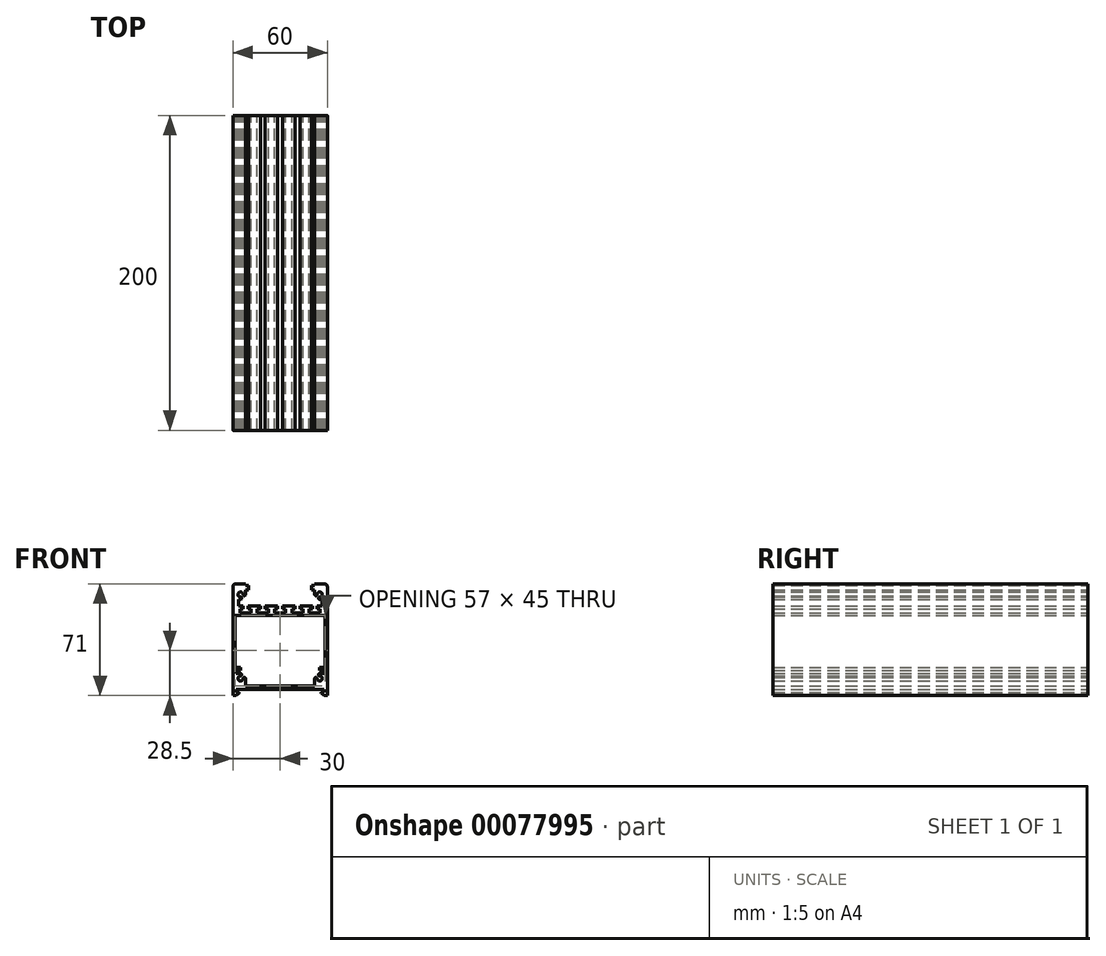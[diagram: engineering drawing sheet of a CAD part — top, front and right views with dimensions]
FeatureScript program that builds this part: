
annotation { "Feature Type Name" : "Feature", "Feature Type Description" : "" }
export const myFeature = defineFeature(function(context is Context, id is Id, definition is map)
    precondition{}
    {
        {
            var Q0;
            Q0=qCreatedBy(makeId("Front.planeOp"),FACE);
            var sketch = newSketch(context, id + "F0", { "sketchPlane" : qUnion([Q0])});
            skLineSegment(sketch, "E0", {"start": v(25.9, -50.3) * mm, "end": v(-25.9, -50.3) * mm});
            skArc(sketch, "E1", {"start": v(-22, -41.64) * mm, "mid": v(-22.75, -40.9) * mm, "end": v(-23.5, -41.64) * mm});
            skLineSegment(sketch, "E2", {"start": v(-22, -41.64) * mm, "end": v(-22, -46.5) * mm});
            skLineSegment(sketch, "E3", {"start": v(-22, -46.5) * mm, "end": v(22, -46.5) * mm});
            skLineSegment(sketch, "E4", {"start": v(22, -46.5) * mm, "end": v(22, -41.64) * mm});
            skArc(sketch, "E5", {"start": v(23.5, -41.64) * mm, "mid": v(22.75, -40.9) * mm, "end": v(22, -41.64) * mm});
            skArc(sketch, "E6", {"start": v(23.5, -41.64) * mm, "mid": v(26.31, -42.81) * mm, "end": v(25.14, -40) * mm});
            skArc(sketch, "E7", {"start": v(25.14, -38.5) * mm, "mid": v(24.4, -39.25) * mm, "end": v(25.14, -40) * mm});
            skLineSegment(sketch, "E8", {"start": v(25.14, -38.5) * mm, "end": v(28, -38.5) * mm});
            skLineSegment(sketch, "E9", {"start": v(28, -38.5) * mm, "end": v(28, -36.5) * mm});
            skLineSegment(sketch, "E10", {"start": v(28, -36.5) * mm, "end": v(25, -36.5) * mm});
            skLineSegment(sketch, "E11", {"start": v(25, -36.5) * mm, "end": v(25, -34.5) * mm});
            skLineSegment(sketch, "E12", {"start": v(25, -34.5) * mm, "end": v(28.5, -34.5) * mm});
            skLineSegment(sketch, "E13", {"start": v(28.5, -34.5) * mm, "end": v(28.5, -1.5) * mm});
            skLineSegment(sketch, "E14", {"start": v(28.5, -1.5) * mm, "end": v(-28.5, -1.5) * mm});
            skLineSegment(sketch, "E15", {"start": v(-28.5, -1.5) * mm, "end": v(-28.5, -34.5) * mm});
            skLineSegment(sketch, "E16", {"start": v(-28.5, -34.5) * mm, "end": v(-25, -34.5) * mm});
            skLineSegment(sketch, "E17", {"start": v(-25, -34.5) * mm, "end": v(-25, -36.5) * mm});
            skLineSegment(sketch, "E18", {"start": v(-25, -36.5) * mm, "end": v(-28, -36.5) * mm});
            skLineSegment(sketch, "E19", {"start": v(-28, -36.5) * mm, "end": v(-28, -38.5) * mm});
            skLineSegment(sketch, "E20", {"start": v(-28, -38.5) * mm, "end": v(-25.14, -38.5) * mm});
            skArc(sketch, "E21", {"start": v(-25.14, -40) * mm, "mid": v(-24.4, -39.25) * mm, "end": v(-25.14, -38.5) * mm});
            skArc(sketch, "E22", {"start": v(-25.14, -40) * mm, "mid": v(-26.31, -42.81) * mm, "end": v(-23.5, -41.64) * mm});
            skLineSegment(sketch, "E23", {"start": v(-22, 18.5) * mm, "end": v(-28, 18.5) * mm});
            skLineSegment(sketch, "E24", {"start": v(-22, 17.5) * mm, "end": v(-22, 18.5) * mm});
            skLineSegment(sketch, "E25", {"start": v(-20, 17.5) * mm, "end": v(-22, 17.5) * mm});
            skLineSegment(sketch, "E26", {"start": v(-20, 14.5) * mm, "end": v(-20, 17.5) * mm});
            skLineSegment(sketch, "E27", {"start": v(-22, 14.5) * mm, "end": v(-20, 14.5) * mm});
            skLineSegment(sketch, "E28", {"start": v(-22, 11.64) * mm, "end": v(-22, 14.5) * mm});
            skArc(sketch, "E29", {"start": v(-23.5, 11.64) * mm, "mid": v(-22.75, 10.9) * mm, "end": v(-22, 11.64) * mm});
            skArc(sketch, "E30", {"start": v(-23.5, 11.64) * mm, "mid": v(-26.31, 12.81) * mm, "end": v(-25.14, 10) * mm});
            skArc(sketch, "E31", {"start": v(-25.14, 8.5) * mm, "mid": v(-24.4, 9.25) * mm, "end": v(-25.14, 10) * mm});
            skLineSegment(sketch, "E32", {"start": v(-26.5, 8.5) * mm, "end": v(-25.14, 8.5) * mm});
            skLineSegment(sketch, "E33", {"start": v(-26.5, 4.5) * mm, "end": v(-26.5, 8.5) * mm});
            skLineSegment(sketch, "E34", {"start": v(-23.5, 4.5) * mm, "end": v(-26.5, 4.5) * mm});
            skLineSegment(sketch, "E35", {"start": v(-23.5, 2.5) * mm, "end": v(-23.5, 4.5) * mm});
            skLineSegment(sketch, "E36", {"start": v(-25.5, 2.5) * mm, "end": v(-23.5, 2.5) * mm});
            skLineSegment(sketch, "E37", {"start": v(-25.5, 0) * mm, "end": v(-25.5, 2.5) * mm});
            skLineSegment(sketch, "E38", {"start": v(-18.5, 0) * mm, "end": v(-25.5, 0) * mm});
            skLineSegment(sketch, "E39", {"start": v(-18.5, 2.5) * mm, "end": v(-18.5, 0) * mm});
            skLineSegment(sketch, "E40", {"start": v(-20.5, 2.5) * mm, "end": v(-18.5, 2.5) * mm});
            skLineSegment(sketch, "E41", {"start": v(-20.5, 4.5) * mm, "end": v(-20.5, 2.5) * mm});
            skLineSegment(sketch, "E42", {"start": v(-12.5, 4.5) * mm, "end": v(-20.5, 4.5) * mm});
            skLineSegment(sketch, "E43", {"start": v(-12.5, 2.5) * mm, "end": v(-12.5, 4.5) * mm});
            skLineSegment(sketch, "E44", {"start": v(-14.5, 2.5) * mm, "end": v(-12.5, 2.5) * mm});
            skLineSegment(sketch, "E45", {"start": v(-14.5, 0) * mm, "end": v(-14.5, 2.5) * mm});
            skLineSegment(sketch, "E46", {"start": v(-7.5, 0) * mm, "end": v(-14.5, 0) * mm});
            skLineSegment(sketch, "E47", {"start": v(-7.5, 2.5) * mm, "end": v(-7.5, 0) * mm});
            skLineSegment(sketch, "E48", {"start": v(-9.5, 2.5) * mm, "end": v(-7.5, 2.5) * mm});
            skLineSegment(sketch, "E49", {"start": v(-9.5, 4.5) * mm, "end": v(-9.5, 2.5) * mm});
            skLineSegment(sketch, "E50", {"start": v(-1.5, 4.5) * mm, "end": v(-9.5, 4.5) * mm});
            skLineSegment(sketch, "E51", {"start": v(-1.5, 2.5) * mm, "end": v(-1.5, 4.5) * mm});
            skLineSegment(sketch, "E52", {"start": v(-3.5, 2.5) * mm, "end": v(-1.5, 2.5) * mm});
            skLineSegment(sketch, "E53", {"start": v(-3.5, 0) * mm, "end": v(-3.5, 2.5) * mm});
            skLineSegment(sketch, "E54", {"start": v(3.5, 0) * mm, "end": v(-3.5, 0) * mm});
            skLineSegment(sketch, "E55", {"start": v(3.5, 2.5) * mm, "end": v(3.5, 0) * mm});
            skLineSegment(sketch, "E56", {"start": v(1.5, 2.5) * mm, "end": v(3.5, 2.5) * mm});
            skLineSegment(sketch, "E57", {"start": v(1.5, 4.5) * mm, "end": v(1.5, 2.5) * mm});
            skLineSegment(sketch, "E58", {"start": v(9.5, 4.5) * mm, "end": v(1.5, 4.5) * mm});
            skLineSegment(sketch, "E59", {"start": v(9.5, 2.5) * mm, "end": v(9.5, 4.5) * mm});
            skLineSegment(sketch, "E60", {"start": v(7.5, 2.5) * mm, "end": v(9.5, 2.5) * mm});
            skLineSegment(sketch, "E61", {"start": v(7.5, 0) * mm, "end": v(7.5, 2.5) * mm});
            skLineSegment(sketch, "E62", {"start": v(14.5, 0) * mm, "end": v(7.5, 0) * mm});
            skLineSegment(sketch, "E63", {"start": v(14.5, 2.5) * mm, "end": v(14.5, 0) * mm});
            skLineSegment(sketch, "E64", {"start": v(12.5, 2.5) * mm, "end": v(14.5, 2.5) * mm});
            skLineSegment(sketch, "E65", {"start": v(12.5, 4.5) * mm, "end": v(12.5, 2.5) * mm});
            skLineSegment(sketch, "E66", {"start": v(20.5, 4.5) * mm, "end": v(12.5, 4.5) * mm});
            skLineSegment(sketch, "E67", {"start": v(20.5, 2.5) * mm, "end": v(20.5, 4.5) * mm});
            skLineSegment(sketch, "E68", {"start": v(18.5, 2.5) * mm, "end": v(20.5, 2.5) * mm});
            skLineSegment(sketch, "E69", {"start": v(18.5, 0) * mm, "end": v(18.5, 2.5) * mm});
            skLineSegment(sketch, "E70", {"start": v(25.5, 0) * mm, "end": v(18.5, 0) * mm});
            skLineSegment(sketch, "E71", {"start": v(25.5, 2.5) * mm, "end": v(25.5, 0) * mm});
            skLineSegment(sketch, "E72", {"start": v(23.5, 2.5) * mm, "end": v(25.5, 2.5) * mm});
            skLineSegment(sketch, "E73", {"start": v(23.5, 4.5) * mm, "end": v(23.5, 2.5) * mm});
            skLineSegment(sketch, "E74", {"start": v(26.5, 4.5) * mm, "end": v(23.5, 4.5) * mm});
            skLineSegment(sketch, "E75", {"start": v(26.5, 8.5) * mm, "end": v(26.5, 4.5) * mm});
            skLineSegment(sketch, "E76", {"start": v(25.14, 8.5) * mm, "end": v(26.5, 8.5) * mm});
            skArc(sketch, "E77", {"start": v(25.14, 10) * mm, "mid": v(24.4, 9.25) * mm, "end": v(25.14, 8.5) * mm});
            skArc(sketch, "E78", {"start": v(25.14, 10) * mm, "mid": v(26.31, 12.81) * mm, "end": v(23.5, 11.64) * mm});
            skArc(sketch, "E79", {"start": v(22, 11.64) * mm, "mid": v(22.75, 10.9) * mm, "end": v(23.5, 11.64) * mm});
            skLineSegment(sketch, "E80", {"start": v(22, 14.5) * mm, "end": v(22, 11.64) * mm});
            skLineSegment(sketch, "E81", {"start": v(20, 14.5) * mm, "end": v(22, 14.5) * mm});
            skLineSegment(sketch, "E82", {"start": v(20, 17.5) * mm, "end": v(20, 14.5) * mm});
            skLineSegment(sketch, "E83", {"start": v(22, 17.5) * mm, "end": v(20, 17.5) * mm});
            skLineSegment(sketch, "E84", {"start": v(22, 18.5) * mm, "end": v(22, 17.5) * mm});
            skLineSegment(sketch, "E85", {"start": v(28, 18.5) * mm, "end": v(22, 18.5) * mm});
            skArc(sketch, "E86", {"start": v(30, 16.5) * mm, "mid": v(29.41, 17.91) * mm, "end": v(28, 18.5) * mm});
            skLineSegment(sketch, "E87", {"start": v(30, -52.5) * mm, "end": v(30, 16.5) * mm});
            skLineSegment(sketch, "E88", {"start": v(28, -52.5) * mm, "end": v(30, -52.5) * mm});
            skLineSegment(sketch, "E89", {"start": v(26.17, -51.23) * mm, "end": v(28, -52.5) * mm});
            skArc(sketch, "E90", {"start": v(26.4, -50.5) * mm, "mid": v(26.02, -50.78) * mm, "end": v(26.17, -51.23) * mm});
            skLineSegment(sketch, "E91", {"start": v(28, -50.5) * mm, "end": v(26.4, -50.5) * mm});
            skLineSegment(sketch, "E92", {"start": v(28, -48.5) * mm, "end": v(28, -50.5) * mm});
            skLineSegment(sketch, "E93", {"start": v(-28, -48.5) * mm, "end": v(28, -48.5) * mm});
            skLineSegment(sketch, "E94", {"start": v(-28, -50.5) * mm, "end": v(-28, -48.5) * mm});
            skLineSegment(sketch, "E95", {"start": v(-26.4, -50.5) * mm, "end": v(-28, -50.5) * mm});
            skArc(sketch, "E96", {"start": v(-26.17, -51.23) * mm, "mid": v(-26.02, -50.78) * mm, "end": v(-26.4, -50.5) * mm});
            skLineSegment(sketch, "E97", {"start": v(-28, -52.5) * mm, "end": v(-26.17, -51.23) * mm});
            skLineSegment(sketch, "E98", {"start": v(-30, -52.5) * mm, "end": v(-28, -52.5) * mm});
            skLineSegment(sketch, "E99", {"start": v(-30, 16.5) * mm, "end": v(-30, -52.5) * mm});
            skArc(sketch, "E100", {"start": v(-28, 18.5) * mm, "mid": v(-29.41, 17.91) * mm, "end": v(-30, 16.5) * mm});
            skLineSegment(sketch, "E101", {"start": v(-12, -57.35) * mm, "end": v(12, -57.35) * mm});
            skLineSegment(sketch, "E102", {"start": v(-7.75, -65.35) * mm, "end": v(-12, -65.35) * mm});
            skLineSegment(sketch, "E103", {"start": v(-7.75, -67.35) * mm, "end": v(-7.75, -65.35) * mm});
            skLineSegment(sketch, "E104", {"start": v(-15.25, -67.35) * mm, "end": v(-7.75, -67.35) * mm});
            skLineSegment(sketch, "E105", {"start": v(-15.25, -65.35) * mm, "end": v(-15.25, -67.35) * mm});
            skLineSegment(sketch, "E106", {"start": v(-12, -65.35) * mm, "end": v(-12, -57.35) * mm});
            skLineSegment(sketch, "E107", {"start": v(-13.78, -62.05) * mm, "end": v(-13.78, -65.35) * mm});
            skLineSegment(sketch, "E108", {"start": v(-20.98, -62.05) * mm, "end": v(-13.78, -62.05) * mm});
            skLineSegment(sketch, "E109", {"start": v(-20.98, -65.35) * mm, "end": v(-20.98, -62.05) * mm});
            skLineSegment(sketch, "E110", {"start": v(-19.5, -65.35) * mm, "end": v(-20.98, -65.35) * mm});
            skLineSegment(sketch, "E111", {"start": v(-19.5, -67.35) * mm, "end": v(-19.5, -65.35) * mm});
            skLineSegment(sketch, "E112", {"start": v(-24, -67.35) * mm, "end": v(-19.5, -67.35) * mm});
            skArc(sketch, "E113", {"start": v(-27.34, -64.77) * mm, "mid": v(-26.11, -66.63) * mm, "end": v(-24, -67.35) * mm});
            skLineSegment(sketch, "E114", {"start": v(-30, -52.5) * mm, "end": v(-27.34, -64.77) * mm});
            skLineSegment(sketch, "E115", {"start": v(-25.9, -52.5) * mm, "end": v(-30, -52.5) * mm});
            skLineSegment(sketch, "E116", {"start": v(-13.78, -65.35) * mm, "end": v(-15.25, -65.35) * mm});
            skLineSegment(sketch, "E117", {"start": v(-26.45, -50.05) * mm, "end": v(-25.9, -50.3) * mm});
            skLineSegment(sketch, "E118", {"start": v(-25.56, -49.15) * mm, "end": v(-26.45, -50.05) * mm});
            skArc(sketch, "E119", {"start": v(-24.7, -49.5) * mm, "mid": v(-25.01, -49.04) * mm, "end": v(-25.56, -49.15) * mm});
            skLineSegment(sketch, "E120", {"start": v(-24.7, -53.7) * mm, "end": v(-24.7, -49.5) * mm});
            skLineSegment(sketch, "E121", {"start": v(-28.51, -53.7) * mm, "end": v(-24.7, -53.7) * mm});
            skLineSegment(sketch, "E122", {"start": v(-26.17, -64.49) * mm, "end": v(-28.51, -53.7) * mm});
            skArc(sketch, "E123", {"start": v(-26.17, -64.49) * mm, "mid": v(-25.37, -65.69) * mm, "end": v(-24, -66.15) * mm});
            skLineSegment(sketch, "E124", {"start": v(-22.48, -66.15) * mm, "end": v(-24, -66.15) * mm});
            skLineSegment(sketch, "E125", {"start": v(-22.48, -60.85) * mm, "end": v(-22.48, -66.15) * mm});
            skLineSegment(sketch, "E126", {"start": v(-13.5, -60.85) * mm, "end": v(-22.48, -60.85) * mm});
            skLineSegment(sketch, "E127", {"start": v(-13.5, -55.85) * mm, "end": v(-13.5, -60.85) * mm});
            skLineSegment(sketch, "E128", {"start": v(13.5, -55.85) * mm, "end": v(-13.5, -55.85) * mm});
            skLineSegment(sketch, "E129", {"start": v(13.5, -60.85) * mm, "end": v(13.5, -55.85) * mm});
            skLineSegment(sketch, "E130", {"start": v(22.48, -60.85) * mm, "end": v(13.5, -60.85) * mm});
            skLineSegment(sketch, "E131", {"start": v(22.48, -66.15) * mm, "end": v(22.48, -60.85) * mm});
            skLineSegment(sketch, "E132", {"start": v(24, -66.15) * mm, "end": v(22.48, -66.15) * mm});
            skArc(sketch, "E133", {"start": v(24, -66.15) * mm, "mid": v(25.37, -65.69) * mm, "end": v(26.17, -64.49) * mm});
            skLineSegment(sketch, "E134", {"start": v(28.51, -53.7) * mm, "end": v(26.17, -64.49) * mm});
            skLineSegment(sketch, "E135", {"start": v(24.7, -53.7) * mm, "end": v(28.51, -53.7) * mm});
            skLineSegment(sketch, "E136", {"start": v(-25.9, -50.3) * mm, "end": v(-25.9, -52.5) * mm});
            skArc(sketch, "E137", {"start": v(25.56, -49.15) * mm, "mid": v(25.01, -49.04) * mm, "end": v(24.7, -49.5) * mm});
            skLineSegment(sketch, "E138", {"start": v(26.45, -50.05) * mm, "end": v(25.56, -49.15) * mm});
            skLineSegment(sketch, "E139", {"start": v(25.9, -50.3) * mm, "end": v(26.45, -50.05) * mm});
            skLineSegment(sketch, "E140", {"start": v(25.9, -52.5) * mm, "end": v(25.9, -50.3) * mm});
            skLineSegment(sketch, "E141", {"start": v(30, -52.5) * mm, "end": v(25.9, -52.5) * mm});
            skLineSegment(sketch, "E142", {"start": v(27.34, -64.77) * mm, "end": v(30, -52.5) * mm});
            skArc(sketch, "E143", {"start": v(24, -67.35) * mm, "mid": v(26.11, -66.63) * mm, "end": v(27.34, -64.77) * mm});
            skLineSegment(sketch, "E144", {"start": v(19.5, -67.35) * mm, "end": v(24, -67.35) * mm});
            skLineSegment(sketch, "E145", {"start": v(19.5, -65.35) * mm, "end": v(19.5, -67.35) * mm});
            skLineSegment(sketch, "E146", {"start": v(20.98, -65.35) * mm, "end": v(19.5, -65.35) * mm});
            skLineSegment(sketch, "E147", {"start": v(20.98, -62.05) * mm, "end": v(20.98, -65.35) * mm});
            skLineSegment(sketch, "E148", {"start": v(13.78, -62.05) * mm, "end": v(20.98, -62.05) * mm});
            skLineSegment(sketch, "E149", {"start": v(13.78, -65.35) * mm, "end": v(13.78, -62.05) * mm});
            skLineSegment(sketch, "E150", {"start": v(15.25, -65.35) * mm, "end": v(13.78, -65.35) * mm});
            skLineSegment(sketch, "E151", {"start": v(15.25, -67.35) * mm, "end": v(15.25, -65.35) * mm});
            skLineSegment(sketch, "E152", {"start": v(7.75, -67.35) * mm, "end": v(15.25, -67.35) * mm});
            skLineSegment(sketch, "E153", {"start": v(7.75, -65.35) * mm, "end": v(7.75, -67.35) * mm});
            skLineSegment(sketch, "E154", {"start": v(12, -65.35) * mm, "end": v(7.75, -65.35) * mm});
            skLineSegment(sketch, "E155", {"start": v(12, -57.35) * mm, "end": v(12, -65.35) * mm});
            skLineSegment(sketch, "E156", {"start": v(24.7, -49.5) * mm, "end": v(24.7, -53.7) * mm});
            skLineSegment(sketch, "E157", {"start": v(-17, -54.74) * mm, "end": v(-13.6, -56.27) * mm});
            skLineSegment(sketch, "E158", {"start": v(39.52, -44.5) * mm, "end": v(41.35, -43.66) * mm});
            skLineSegment(sketch, "E159", {"start": v(-26, -50.9) * mm, "end": v(-26, -51.4) * mm});
            skLineSegment(sketch, "E160", {"start": v(26, -50.9) * mm, "end": v(26, -52.22) * mm});
            skSolve(sketch);
        }
        {
            var Q0;
            Q0=makeQuery(id+"F0.imprint","IMPRINT",FACE,{"disambiguationData":[TD([[makeQuery(id+"F0.imprint","IMPRINT",EDGE,{"derivedFrom":sQuery(id+"F0.wireOp",EDGE,"E1")}),1.0]])]});
            extrude(context, id + "F1", {"entities" : qUnion([Q0]), "depth" : 200 * mm});
        }
    });
